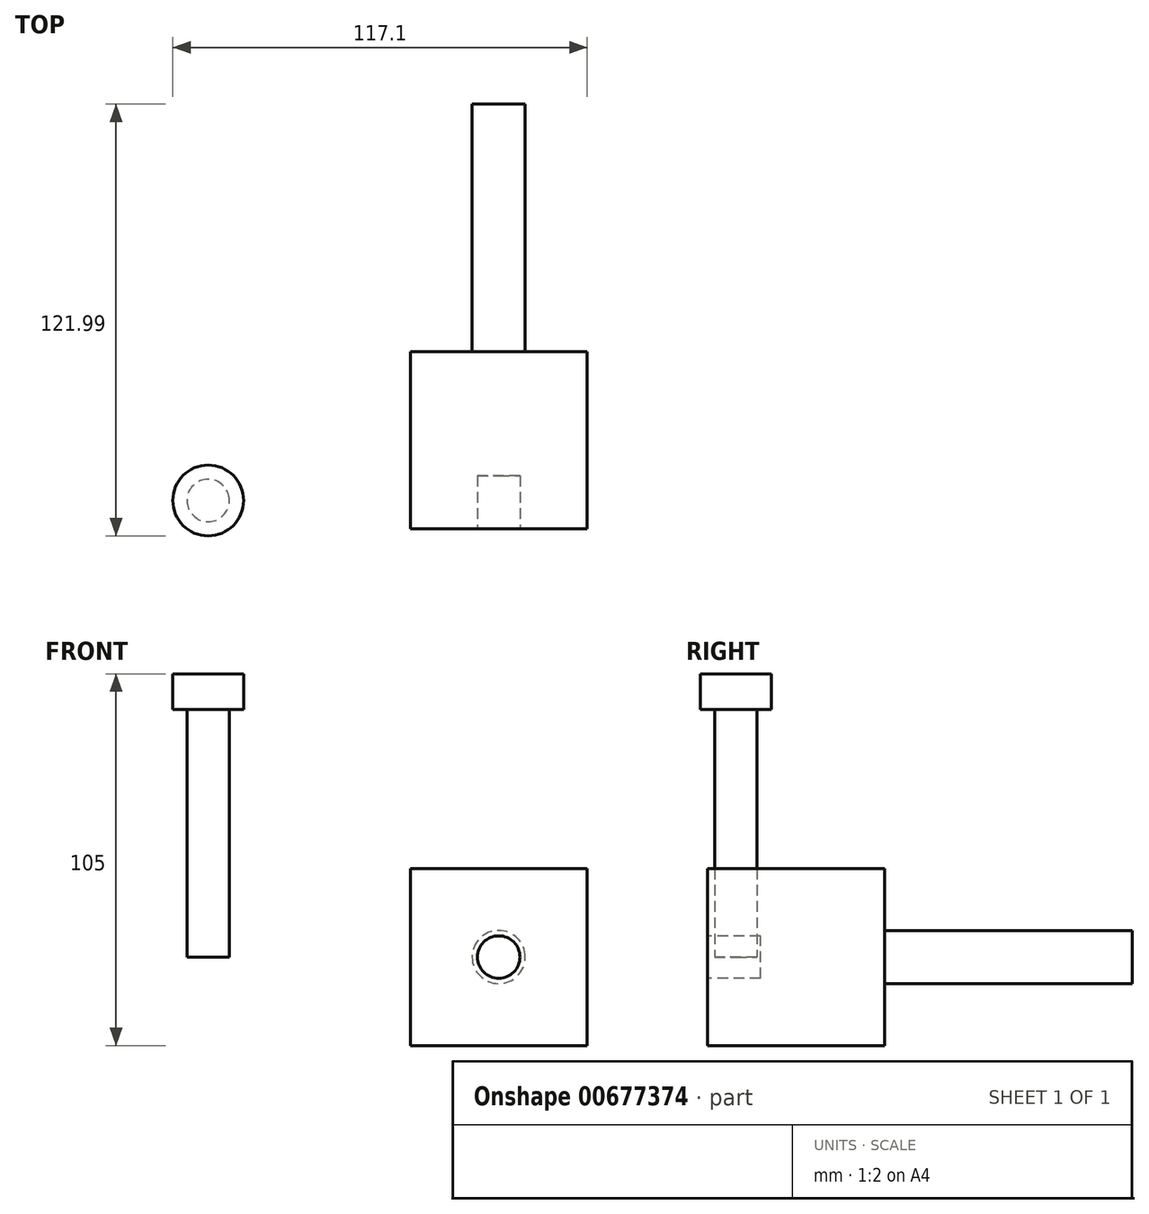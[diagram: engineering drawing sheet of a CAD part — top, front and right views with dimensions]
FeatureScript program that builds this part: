
annotation { "Feature Type Name" : "Feature", "Feature Type Description" : "" }
export const myFeature = defineFeature(function(context is Context, id is Id, definition is map)
    precondition{}
    {
        {
            var Q0;
            Q0=qCreatedBy(makeId("Front.planeOp"),FACE);
            var sketch = newSketch(context, id + "F0", { "sketchPlane" : qUnion([Q0])});
            skLineSegment(sketch, "E0.bottom", {"start": v(25, 25) * mm, "end": v(-25, 25) * mm});
            skLineSegment(sketch, "E0.top", {"start": v(25, -25) * mm, "end": v(-25, -25) * mm});
            skLineSegment(sketch, "E0.left", {"start": v(25, 25) * mm, "end": v(25, -25) * mm});
            skLineSegment(sketch, "E0.right", {"start": v(-25, 25) * mm, "end": v(-25, -25) * mm});
            skPoint(sketch, "E0.middle", {"position": v(0, 0) * mm});
            skCircle(sketch, "E1", {"center": v(0, 0) * mm, "radius": 7.5 * mm});
            skSolve(sketch);
        }
        {
            var Q0;
            Q0=makeQuery(id+"F0.imprint","IMPRINT",FACE,{"disambiguationData":[TD([[makeQuery(id+"F0.imprint","IMPRINT",EDGE,{"derivedFrom":sQuery(id+"F0.wireOp",EDGE,"E1")}),1.0]])]});
            var Q1;
            Q1=makeQuery(id+"F0.imprint","IMPRINT",FACE,{"disambiguationData":[TD([[makeQuery(id+"F0.imprint","IMPRINT",EDGE,{"derivedFrom":sQuery(id+"F0.wireOp",EDGE,"E0.bottom")}),1.0]])]});
            extrude(context, id + "F1", {"entities" : qUnion([Q0, Q1]), "depth" : 50 * mm, "offsetDistance" : 25 * mm});
        }
        {
            var Q0;
            Q0=makeQuery(id+"F0.imprint","IMPRINT",FACE,{"disambiguationData":[TD([[makeQuery(id+"F0.imprint","IMPRINT",EDGE,{"derivedFrom":sQuery(id+"F0.wireOp",EDGE,"E1")}),1.0]])]});
            var Q1;
            Q1=sQuery(id+"F0.wireOp",EDGE,"E1");
            extrude(context, id + "F2", {"entities" : qUnion([Q0]), "operationType" : NewBodyOperationType.ADD, "surfaceEntities" : qUnion([Q1]), "oppositeDirection" : true, "depth" : 70 * mm, "offsetDistance" : 25 * mm});
        }
        {
            var Q0;
            Q0=makeQuery(id+"F1.opExtrude","CAP_FACE",FACE,{"disambiguationData":[OSD([sQuery(id+"F0.wireOp",EDGE,"E0.bottom"),sQuery(id+"F0.wireOp",EDGE,"E0.top"),sQuery(id+"F0.wireOp",EDGE,"E0.left"),sQuery(id+"F0.wireOp",EDGE,"E0.right")])],"isStart":false});
            var sketch = newSketch(context, id + "F3", { "sketchPlane" : qUnion([Q0])});
            skCircle(sketch, "E2", {"center": v(0, 0) * mm, "radius": 6 * mm});
            skSolve(sketch);
        }
        {
            var Q0;
            Q0 = qSketchRegion(id + "F3", true);
            extrude(context, id + "F4", {"entities" : qUnion([Q0]), "operationType" : NewBodyOperationType.REMOVE, "oppositeDirection" : true, "depth" : 15 * mm, "offsetDistance" : 25 * mm});
        }
        {
            var Q0;
            Q0=qCreatedBy(makeId("Top.planeOp"),FACE);
            var sketch = newSketch(context, id + "F5", { "sketchPlane" : qUnion([Q0])});
            skCircle(sketch, "E3", {"center": v(-82.1, -42) * mm, "radius": 6 * mm});
            skSolve(sketch);
        }
        {
            var Q0;
            Q0 = qSketchRegion(id + "F5", true);
            extrude(context, id + "F6", {"entities" : qUnion([Q0]), "depth" : 70 * mm, "offsetDistance" : 25 * mm});
        }
        {
            var Q0;
            Q0=makeQuery(id+"F6.opExtrude","CAP_FACE",FACE,{"disambiguationData":[OSD([sQuery(id+"F5.wireOp",EDGE,"E3")])],"isStart":false});
            var sketch = newSketch(context, id + "F7", { "sketchPlane" : qUnion([Q0])});
            skCircle(sketch, "E4.0.0", {"center": v(-82.1, -42) * mm, "radius": 6 * mm});
            skCircle(sketch, "E5", {"center": v(-82.1, -42) * mm, "radius": 10 * mm});
            skSolve(sketch);
        }
        {
            var Q0;
            Q0 = qSketchRegion(id + "F7", true);
            var Q1;
            Q1=makeQuery(id+"F7.imprint","IMPRINT",FACE,{"disambiguationData":[TD([[makeQuery(id+"F7.imprint","IMPRINT",EDGE,{"derivedFrom":sQuery(id+"F7.wireOp",EDGE,"E4.0.0")}),1.0]])]});
            extrude(context, id + "F8", {"entities" : qUnion([Q0, Q1]), "operationType" : NewBodyOperationType.ADD, "depth" : 10 * mm, "offsetDistance" : 25 * mm});
        }
    });
